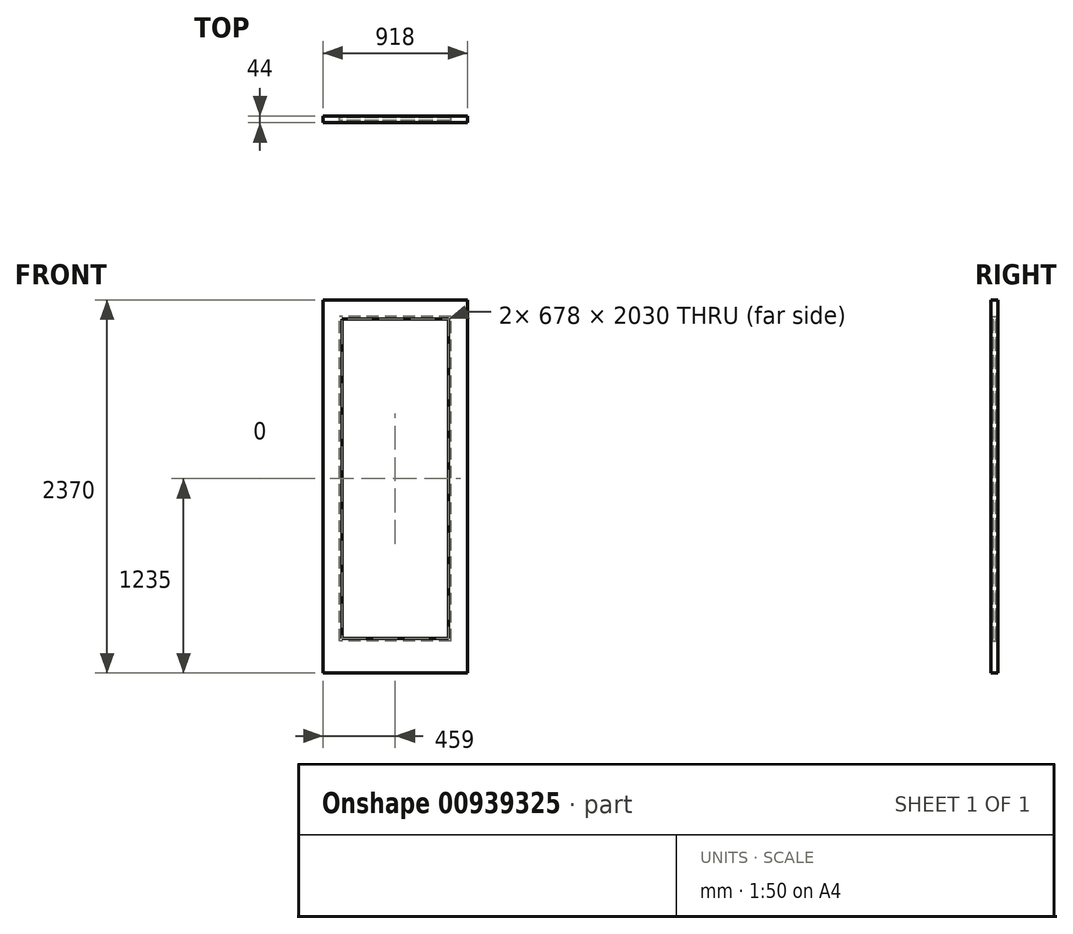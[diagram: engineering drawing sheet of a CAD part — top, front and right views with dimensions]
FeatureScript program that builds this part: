
annotation { "Feature Type Name" : "Feature", "Feature Type Description" : "" }
export const myFeature = defineFeature(function(context is Context, id is Id, definition is map)
    precondition{}
    {
        {
            var Q0;
            Q0=qCreatedBy(makeId("Front.planeOp"),FACE);
            var sketch = newSketch(context, id + "F0", { "sketchPlane" : qUnion([Q0])});
            skLineSegment(sketch, "E0.bottom", {"start": v(0, 0) * mm, "end": v(-918, 0) * mm});
            skLineSegment(sketch, "E0.top", {"start": v(0, 2370) * mm, "end": v(-918, 2370) * mm});
            skLineSegment(sketch, "E0.left", {"start": v(0, 0) * mm, "end": v(0, 2370) * mm});
            skLineSegment(sketch, "E0.right", {"start": v(-918, 0) * mm, "end": v(-918, 2370) * mm});
            skLineSegment(sketch, "E1.bottom", {"start": v(-120, 2250) * mm, "end": v(-798, 2250) * mm});
            skLineSegment(sketch, "E1.top", {"start": v(-120, 220) * mm, "end": v(-798, 220) * mm});
            skLineSegment(sketch, "E1.left", {"start": v(-120, 2250) * mm, "end": v(-120, 220) * mm});
            skLineSegment(sketch, "E1.right", {"start": v(-798, 2250) * mm, "end": v(-798, 220) * mm});
            skSolve(sketch);
        }
        {
            var Q0;
            Q0 = qSketchRegion(id + "F0", true);
            extrude(context, id + "F1", {"entities" : qUnion([Q0]), "depth" : 44 * mm, "offsetDistance" : 25 * mm});
        }
        {
            var Q0;
            Q0=makeQuery(id+"F1.opExtrude","CAP_FACE",FACE,{"disambiguationData":[OSD([sQuery(id+"F0.wireOp",EDGE,"E0.bottom"),sQuery(id+"F0.wireOp",EDGE,"E0.top"),sQuery(id+"F0.wireOp",EDGE,"E0.left"),sQuery(id+"F0.wireOp",EDGE,"E0.right"),sQuery(id+"F0.wireOp",EDGE,"E1.bottom"),sQuery(id+"F0.wireOp",EDGE,"E1.top"),sQuery(id+"F0.wireOp",EDGE,"E1.left"),sQuery(id+"F0.wireOp",EDGE,"E1.right")])],"isStart":true});
            var sketch = newSketch(context, id + "F2", { "sketchPlane" : qUnion([Q0])});
            skLineSegment(sketch, "E2.bottom", {"start": v(120, 220) * mm, "end": v(798, 220) * mm});
            skLineSegment(sketch, "E2.top", {"start": v(120, 2250) * mm, "end": v(798, 2250) * mm});
            skLineSegment(sketch, "E2.left", {"start": v(120, 220) * mm, "end": v(120, 2250) * mm});
            skLineSegment(sketch, "E2.right", {"start": v(798, 220) * mm, "end": v(798, 2250) * mm});
            skLineSegment(sketch, "E3.0", {"start": v(105, 2265) * mm, "end": v(813, 2265) * mm});
            skLineSegment(sketch, "E3.1", {"start": v(105, 205) * mm, "end": v(105, 2265) * mm});
            skLineSegment(sketch, "E3.2", {"start": v(105, 205) * mm, "end": v(813, 205) * mm});
            skLineSegment(sketch, "E3.3", {"start": v(813, 205) * mm, "end": v(813, 2265) * mm});
            skSolve(sketch);
        }
        {
            var Q0;
            Q0 = qSketchRegion(id + "F2", true);
            extrude(context, id + "F3", {"entities" : qUnion([Q0]), "operationType" : NewBodyOperationType.REMOVE, "oppositeDirection" : true, "depth" : 31 * mm, "offsetDistance" : 25 * mm});
        }
        {
            var Q0;
            Q0=makeQuery(id+"F1.opExtrude","CAP_FACE",FACE,{"disambiguationData":[OSD([sQuery(id+"F0.wireOp",EDGE,"E0.bottom"),sQuery(id+"F0.wireOp",EDGE,"E0.top"),sQuery(id+"F0.wireOp",EDGE,"E0.left"),sQuery(id+"F0.wireOp",EDGE,"E0.right"),sQuery(id+"F0.wireOp",EDGE,"E1.bottom"),sQuery(id+"F0.wireOp",EDGE,"E1.top"),sQuery(id+"F0.wireOp",EDGE,"E1.left"),sQuery(id+"F0.wireOp",EDGE,"E1.right")])],"isStart":true});
            var sketch = newSketch(context, id + "F4", { "sketchPlane" : qUnion([Q0])});
            skLineSegment(sketch, "E4.bottom", {"start": v(105, 2265) * mm, "end": v(813, 2265) * mm});
            skLineSegment(sketch, "E4.top", {"start": v(105, 205) * mm, "end": v(813, 205) * mm});
            skLineSegment(sketch, "E4.left", {"start": v(105, 2265) * mm, "end": v(105, 205) * mm});
            skLineSegment(sketch, "E4.right", {"start": v(813, 2265) * mm, "end": v(813, 205) * mm});
            skLineSegment(sketch, "E5.0", {"start": v(120, 2250) * mm, "end": v(120, 220) * mm});
            skLineSegment(sketch, "E5.1", {"start": v(120, 2250) * mm, "end": v(798, 2250) * mm});
            skLineSegment(sketch, "E5.2", {"start": v(798, 2250) * mm, "end": v(798, 220) * mm});
            skLineSegment(sketch, "E5.3", {"start": v(120, 220) * mm, "end": v(798, 220) * mm});
            skSolve(sketch);
        }
        {
            var Q0;
            Q0 = qSketchRegion(id + "F4", true);
            extrude(context, id + "F5", {"entities" : qUnion([Q0]), "oppositeDirection" : true, "depth" : 12 * mm, "offsetDistance" : 25 * mm});
        }
    });
